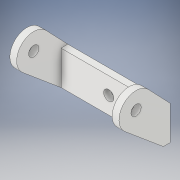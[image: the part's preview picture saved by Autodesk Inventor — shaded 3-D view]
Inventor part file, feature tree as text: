
AUTODESK INVENTOR PART (.ipt)
format: ipt  version: 2017 SP1 (Build 210196100, 196)  size: 138,752 bytes
history: native  units: in
note: dims shown in document units (in); Inventor stores cm internally (conversion verified against a paired STEP export)
features: extrude x4, sketch x4, projected_geometry x1
ambient origin geometry x8: Origin, YZ Plane, XZ Plane, XY Plane, X Axis, Y Axis, Z Axis, Center Point
bodies: Solid1 (feature_tree)
feature tree (9):
  extrude  "Extrusion1"  Depth=0.3937in
  extrude  "Extrusion2"  Depth=0.0787in
  extrude  "Extrusion3"  Depth=0.3937in
  extrude  "Extrusion4"  Depth=0.0787in
  sketch  "Sketch1"  dims[d0=1.2598in d1=0.3937in]
  sketch  "Sketch2"  dims[d2=0.0787in d3=0.0in d4=0.1181in]
  sketch  "Sketch3"  dims[d5=0.0787in d6=0.0in d7=0.3937in]
  sketch  "Sketch4"  dims[d8=0.3937in d9=0.3436in d10=0.1181in d11=0.0787in d12=0.0in d13=0.0787in d14=0.0in]
  projected_geometry  "Projected Loop1"
